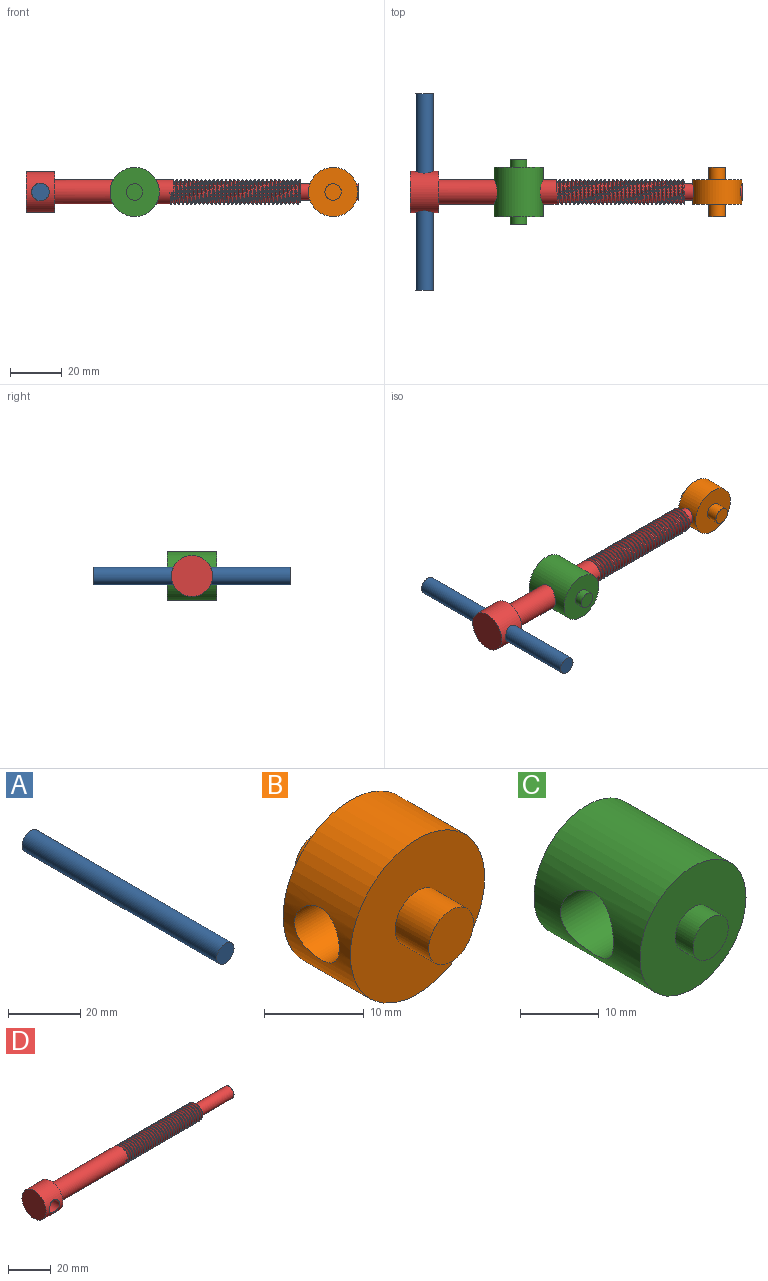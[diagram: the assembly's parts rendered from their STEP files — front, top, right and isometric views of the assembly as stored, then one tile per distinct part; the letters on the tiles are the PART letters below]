
ASSEMBLY  parts=4 mates=4
PART A: 3 faces, bbox 6.8x76.2x6.8 mm
  f0: cylinder r=3.38mm len=76.2mm, axis (0,1,0), area 1617.4mm2, adj f1,f2
  f1: plane 6.76x6.76mm, normal (0,-1,0), area 35.9mm2, adj f0
  f2: plane 6.76x6.76mm, normal (0,1,0), area 35.9mm2, adj f0
PART B: 8 faces, bbox 19.1x19.1x19.1 mm
  f0: cylinder r=3.17mm len=6.35mm, axis (0,1,0), area 95mm2, adj f1,f3
  f1: plane 6.35x6.35mm, normal (0,-1,0), area 31.7mm2, adj f0
  f2: cylinder r=9.53mm len=19.05mm, axis (0,1,0), area 505.7mm2, adj f3,f4,f7
  f3: plane 19.05x19.05mm, normal (0,-1,0), area 253.4mm2, adj f0,f2
  f4: plane 19.05x19.05mm, normal (0,1,0), area 253.4mm2, adj f2,f6
  f5: plane 6.35x6.35mm, normal (0,1,0), area 31.7mm2, adj f6
  f6: cylinder r=3.17mm len=6.35mm, axis (0,1,0), area 95mm2, adj f4,f5
  f7: cylinder r=3.17mm len=19.05mm, axis (1,0,0), area 369.2mm2, adj f2
PART C: 8 faces, bbox 19.1x25.4x19.1 mm
  f0: cylinder r=9.53mm len=19.05mm, axis (0,1,0), area 992.4mm2, adj f3,f4,f7
  f1: cylinder r=3.17mm len=6.35mm, axis (0,1,0), area 63.3mm2, adj f2,f3
  f2: plane 6.35x6.35mm, normal (0,-1,0), area 31.7mm2, adj f1
  f3: plane 19.05x19.05mm, normal (0,-1,0), area 253.4mm2, adj f0,f1
  f4: plane 19.05x19.05mm, normal (0,1,0), area 253.4mm2, adj f0,f6
  f5: plane 6.35x6.35mm, normal (0,1,0), area 31.7mm2, adj f6
  f6: cylinder r=3.17mm len=6.35mm, axis (0,1,0), area 63.3mm2, adj f4,f5
  f7: cylinder r=4.76mm len=19.05mm, axis (-1,0,0), area 532.5mm2, adj f0
PART D: 43 faces, bbox 129.1x16.4x16.4 mm
  f0: cylinder r=4.78mm len=47.4mm, axis (-1,0,0), area 1366.7mm2, adj f31,f37,f39,f40,f41
  f1: cylinder r=4.78mm len=5.09mm, axis (-1,0,0), area 1.1mm2, adj f2,f36,f39,f40
  f2: cylinder r=4.78mm len=9.55mm, axis (-1,0,0), area 5.5mm2, adj f1,f3,f39,f40
  f3: cylinder r=4.78mm len=9.55mm, axis (-1,0,0), area 5.5mm2, adj f2,f4,f39,f40
  f4: cylinder r=4.78mm len=9.55mm, axis (-1,0,0), area 5.5mm2, adj f3,f5,f39,f40
  f5: cylinder r=4.78mm len=9.55mm, axis (-1,0,0), area 5.5mm2, adj f4,f6,f39,f40
  f6: cylinder r=4.78mm len=9.55mm, axis (-1,0,0), area 5.5mm2, adj f5,f7,f39,f40
  f7: cylinder r=4.78mm len=9.55mm, axis (-1,0,0), area 5.5mm2, adj f6,f8,f39,f40
  f8: cylinder r=4.78mm len=9.55mm, axis (-1,0,0), area 5.5mm2, adj f7,f9,f39,f40
  f9: cylinder r=4.78mm len=9.55mm, axis (-1,0,0), area 5.5mm2, adj f8,f10,f39,f40
  f10: cylinder r=4.78mm len=9.55mm, axis (-1,0,0), area 5.5mm2, adj f9,f11,f39,f40
  f11: cylinder r=4.78mm len=9.55mm, axis (-1,0,0), area 5.5mm2, adj f10,f12,f39,f40
  f12: cylinder r=4.78mm len=9.55mm, axis (-1,0,0), area 5.5mm2, adj f11,f13,f39,f40
  f13: cylinder r=4.78mm len=9.55mm, axis (-1,0,0), area 5.5mm2, adj f12,f14,f39,f40
  f14: cylinder r=4.78mm len=9.55mm, axis (-1,0,0), area 5.5mm2, adj f13,f15,f39,f40
  f15: cylinder r=4.78mm len=9.55mm, axis (-1,0,0), area 5.5mm2, adj f14,f16,f39,f40
  f16: cylinder r=4.78mm len=9.55mm, axis (-1,0,0), area 5.5mm2, adj f15,f17,f39,f40
  f17: cylinder r=4.78mm len=9.55mm, axis (-1,0,0), area 5.5mm2, adj f16,f18,f39,f40
  f18: cylinder r=4.78mm len=9.55mm, axis (-1,0,0), area 5.5mm2, adj f17,f19,f39,f40
  f19: cylinder r=4.78mm len=9.55mm, axis (-1,0,0), area 5.5mm2, adj f18,f20,f39,f40
  f20: cylinder r=4.78mm len=9.55mm, axis (-1,0,0), area 5.5mm2, adj f19,f21,f39,f40
  f21: cylinder r=4.78mm len=9.55mm, axis (-1,0,0), area 5.5mm2, adj f20,f22,f39,f40
  f22: cylinder r=4.78mm len=9.55mm, axis (-1,0,0), area 5.5mm2, adj f21,f23,f39,f40
  f23: cylinder r=4.78mm len=9.55mm, axis (-1,0,0), area 5.5mm2, adj f22,f24,f39,f40
  f24: cylinder r=4.78mm len=9.55mm, axis (-1,0,0), area 5.5mm2, adj f23,f25,f39,f40
  f25: cylinder r=4.78mm len=9.55mm, axis (-1,0,0), area 5.5mm2, adj f24,f26,f39,f40
  f26: cylinder r=4.78mm len=9.55mm, axis (-1,0,0), area 5.5mm2, adj f25,f27,f39,f40
  f27: cylinder r=4.78mm len=9.55mm, axis (-1,0,0), area 5.5mm2, adj f26,f28,f39,f40
  f28: cylinder r=4.78mm len=9.55mm, axis (-1,0,0), area 5.5mm2, adj f27,f29,f39,f40
  f29: cylinder r=4.78mm len=9.55mm, axis (-1,0,0), area 5.5mm2, adj f28,f30,f39,f40
  f30: cylinder r=4.78mm len=9.55mm, axis (-1,0,0), area 5.5mm2, adj f29,f31,f39,f40
  f31: cylinder r=4.78mm len=9.55mm, axis (-1,0,0), area 5.5mm2, adj f0,f30,f39,f40
  f32: cylinder r=7.95mm len=15.9mm, axis (-1,0,0), area 482.3mm2, adj f33,f37,f42
  f33: plane 15.9x15.9mm, normal (-1,0,0), area 198.6mm2, adj f32
  f34: plane 6.35x6.35mm, normal (1,0,0), area 31.7mm2, adj f35
  f35: cylinder r=3.17mm len=22.23mm, axis (-1,0,0), area 443.4mm2, adj f34,f36
  f36: plane 9.14x9mm, normal (1,0,0), area 26.3mm2, adj f1,f35,f38,f39,f40
  f37: plane 15.9x15.9mm, normal (1,0,0), area 126.9mm2, adj f0,f32
  f38: cylinder r=3.91mm len=50.13mm, axis (1,0,0), area 152.9mm2, adj f36,f39,f40,f41
  f39: bspline ~51.3x11.03mm, area 865.3mm2, adj f0,f1,f2,f3,f4,f5,f6,f7
  f40: bspline ~50.24x11.03mm, area 849.2mm2, adj f0,f1,f2,f3,f4,f5,f6,f7
  f41: plane 1.4x0.86mm, normal (0,0,-1), area 0.8mm2, adj f0,f38,f39,f40
  f42: cylinder r=3.38mm len=14.39mm, axis (0,-1,0), area 305.5mm2, adj f32
PLACE A t=(92.21,61.21,-20.75)mm
PLACE B t=(221.89,61.21,-20.75)mm
PLACE C t=(-76.29,61.21,-20.75)mm
PLACE D t=(78.95,61.21,-20.75)mm
MATE revolute B.f7 <-> D.f0  axis (1,0,0) through (207.55,61.21,-20.75)mm
MATE slider B.f7 <-> D.f0  axis (1,0,0) through (197.9,61.21,-20.75)mm
MATE cylindrical C.f7 <-> D.f0  axis (-1,0,0) through (130.68,61.21,-20.75)mm
MATE fastened A.f0 <-> D.f42  axis (0,1,0) through (84.51,61.21,-20.75)mm
